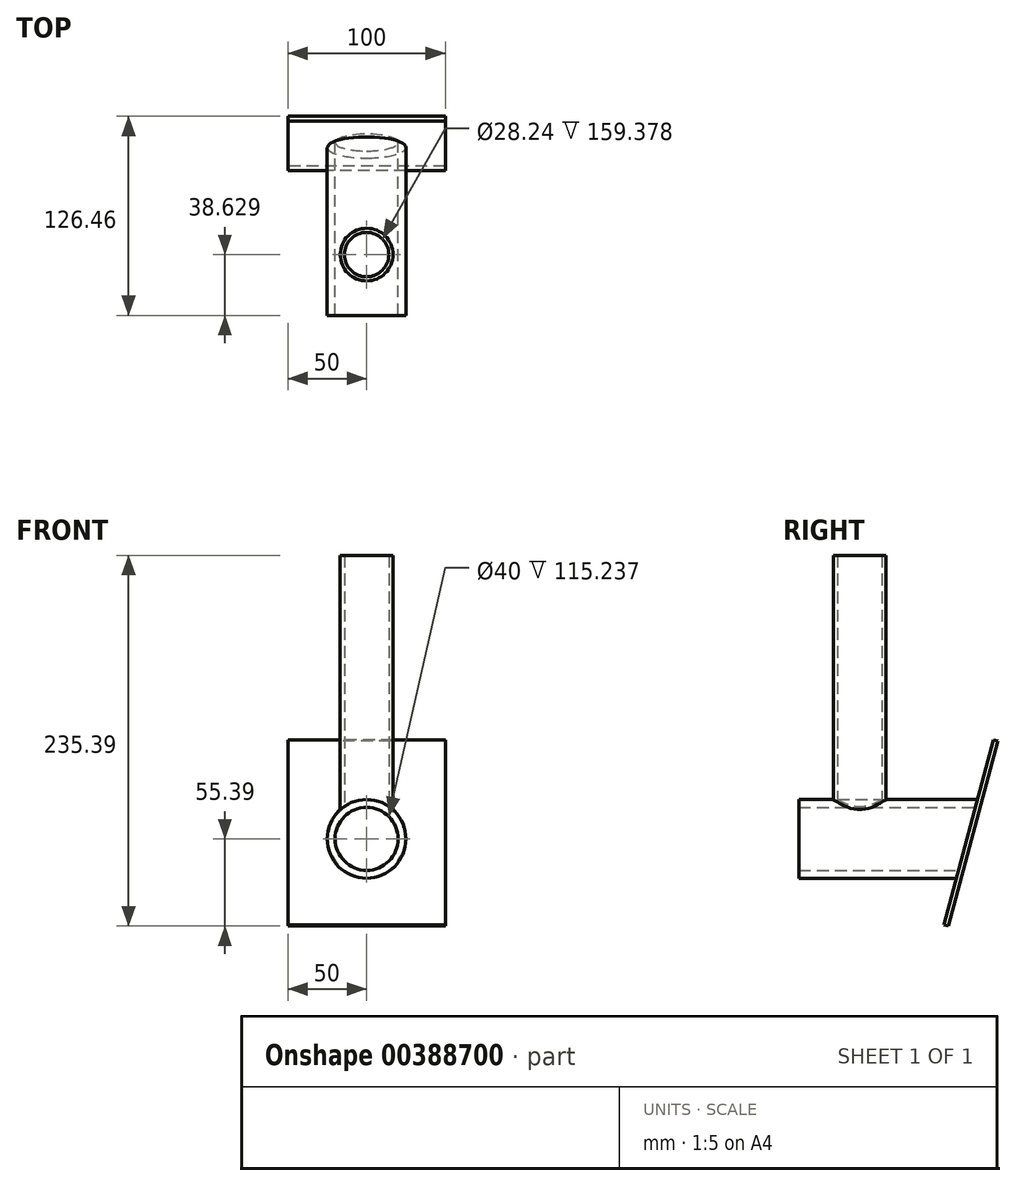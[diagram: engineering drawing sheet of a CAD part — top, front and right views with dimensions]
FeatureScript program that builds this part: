
annotation { "Feature Type Name" : "Feature", "Feature Type Description" : "" }
export const myFeature = defineFeature(function(context is Context, id is Id, definition is map)
    precondition{}
    {
        {
            var Q0;
            Q0=qCreatedBy(makeId("Front.planeOp"),FACE);
            var sketch = newSketch(context, id + "F0", { "sketchPlane" : qUnion([Q0])});
            skLineSegment(sketch, "E0.bottom", {"start": v(47.5, 65) * mm, "end": v(-47.5, 65) * mm});
            skLineSegment(sketch, "E0.top", {"start": v(47.5, -65) * mm, "end": v(-47.5, -65) * mm});
            skLineSegment(sketch, "E0.left", {"start": v(47.5, 65) * mm, "end": v(47.5, -65) * mm});
            skLineSegment(sketch, "E0.right", {"start": v(-47.5, 65) * mm, "end": v(-47.5, -65) * mm});
            skPoint(sketch, "E0.middle", {"position": v(0, 0) * mm});
            skCircle(sketch, "E1", {"center": v(0, 0) * mm, "radius": 25 * mm});
            skCircle(sketch, "E2", {"center": v(0, 0) * mm, "radius": 20 * mm});
            skSolve(sketch);
        }
        {
            var Q0;
            Q0=makeQuery(id+"F0.imprint","IMPRINT",FACE,{"disambiguationData":[TD([[makeQuery(id+"F0.imprint","IMPRINT",EDGE,{"derivedFrom":sQuery(id+"F0.wireOp",EDGE,"E1")}),1.0]])]});
            extrude(context, id + "F1", {"entities" : qUnion([Q0]), "depth" : 100 * mm});
        }
        {
            var Q0;
            Q0=qCreatedBy(makeId("Top.planeOp"),FACE);
            var sketch = newSketch(context, id + "F2", { "sketchPlane" : qUnion([Q0])});
            skCircle(sketch, "E3", {"center": v(0, -61.37) * mm, "radius": 16.73 * mm});
            skCircle(sketch, "E4", {"center": v(0, -61.37) * mm, "radius": 14.12 * mm});
            skSolve(sketch);
        }
        {
            var Q0;
            Q0 = qSketchRegion(id + "F2", true);
            extrude(context, id + "F3", {"entities" : qUnion([Q0]), "operationType" : NewBodyOperationType.ADD, "depth" : 180 * mm, "hasSecondDirection" : true, "secondDirectionBound" : SecondDirectionBoundingType.UP_TO_NEXT, "secondDirectionOppositeDirection" : false, "secondDirectionDepth" : 100 * mm});
        }
        {
            var Q0;
            Q0=qCreatedBy(makeId("Right.planeOp"),FACE);
            var sketch = newSketch(context, id + "F4", { "sketchPlane" : qUnion([Q0])});
            skLineSegment(sketch, "E5", {"start": v(0, -25) * mm, "end": v(-100, -25) * mm});
            skLineSegment(sketch, "E6.0", {"start": v(0, -25) * mm, "end": v(0, 25) * mm});
            skLineSegment(sketch, "E7", {"start": v(-7.94, -54.62) * mm, "end": v(23.56, 62.92) * mm});
            skLineSegment(sketch, "E8.0", {"start": v(-5.04, -55.4) * mm, "end": v(26.46, 62.15) * mm});
            skLineSegment(sketch, "E9", {"start": v(23.56, 62.92) * mm, "end": v(26.46, 62.15) * mm});
            skLineSegment(sketch, "E10", {"start": v(-7.94, -54.62) * mm, "end": v(-5.04, -55.4) * mm});
            skSolve(sketch);
        }
        {
            var Q0;
            Q0=makeQuery(id+"F4.imprint","IMPRINT",FACE,{"disambiguationData":[TD([[makeQuery(id+"F4.imprint","IMPRINT",EDGE,{"derivedFrom":sQuery(id+"F4.wireOp",EDGE,"E8.0")}),1.0]])]});
            extrude(context, id + "F5", {"entities" : qUnion([Q0]), "endBound" : BoundingType.SYMMETRIC, "depth" : 100 * mm});
        }
        {
            var Q0;
            Q0=makeQuery(id+"F0.imprint","IMPRINT",FACE,{"disambiguationData":[TD([[makeQuery(id+"F0.imprint","IMPRINT",EDGE,{"derivedFrom":sQuery(id+"F0.wireOp",EDGE,"E1")}),1.0]])]});
            var Q1;
            Q1=makeQuery(id+"F5.opExtrude","SWEPT_FACE",FACE,{"disambiguationData":[OSD([sQuery(id+"F4.wireOp",EDGE,"E7")])]});
            extrude(context, id + "F6", {"entities" : qUnion([Q0]), "operationType" : NewBodyOperationType.ADD, "endBound" : BoundingType.UP_TO_SURFACE, "oppositeDirection" : true, "endBoundEntityFace" : qUnion([Q1]), "depth" : 25 * mm});
        }
        {
            var Q0;
            Q0=makeQuery(id+"F1.opExtrude","CAP_FACE",FACE,{"disambiguationData":[OSD([sQuery(id+"F0.wireOp",EDGE,"E1"),sQuery(id+"F0.wireOp",EDGE,"E2")])],"isStart":false});
            var sketch = newSketch(context, id + "F7", { "sketchPlane" : qUnion([Q0])});
            skCircle(sketch, "E11", {"center": v(0, 0) * mm, "radius": 20 * mm});
            skSolve(sketch);
        }
        {
            var Q0;
            Q0=makeQuery(id+"F7.imprint","IMPRINT",FACE,{"disambiguationData":[TD([[makeQuery(id+"F7.imprint","IMPRINT",EDGE,{"derivedFrom":sQuery(id+"F7.wireOp",EDGE,"E11")}),1.0]])]});
            extrude(context, id + "F8", {"entities" : qUnion([Q0]), "operationType" : NewBodyOperationType.REMOVE, "endBound" : BoundingType.THROUGH_ALL, "oppositeDirection" : true, "depth" : 25 * mm});
        }
    });
